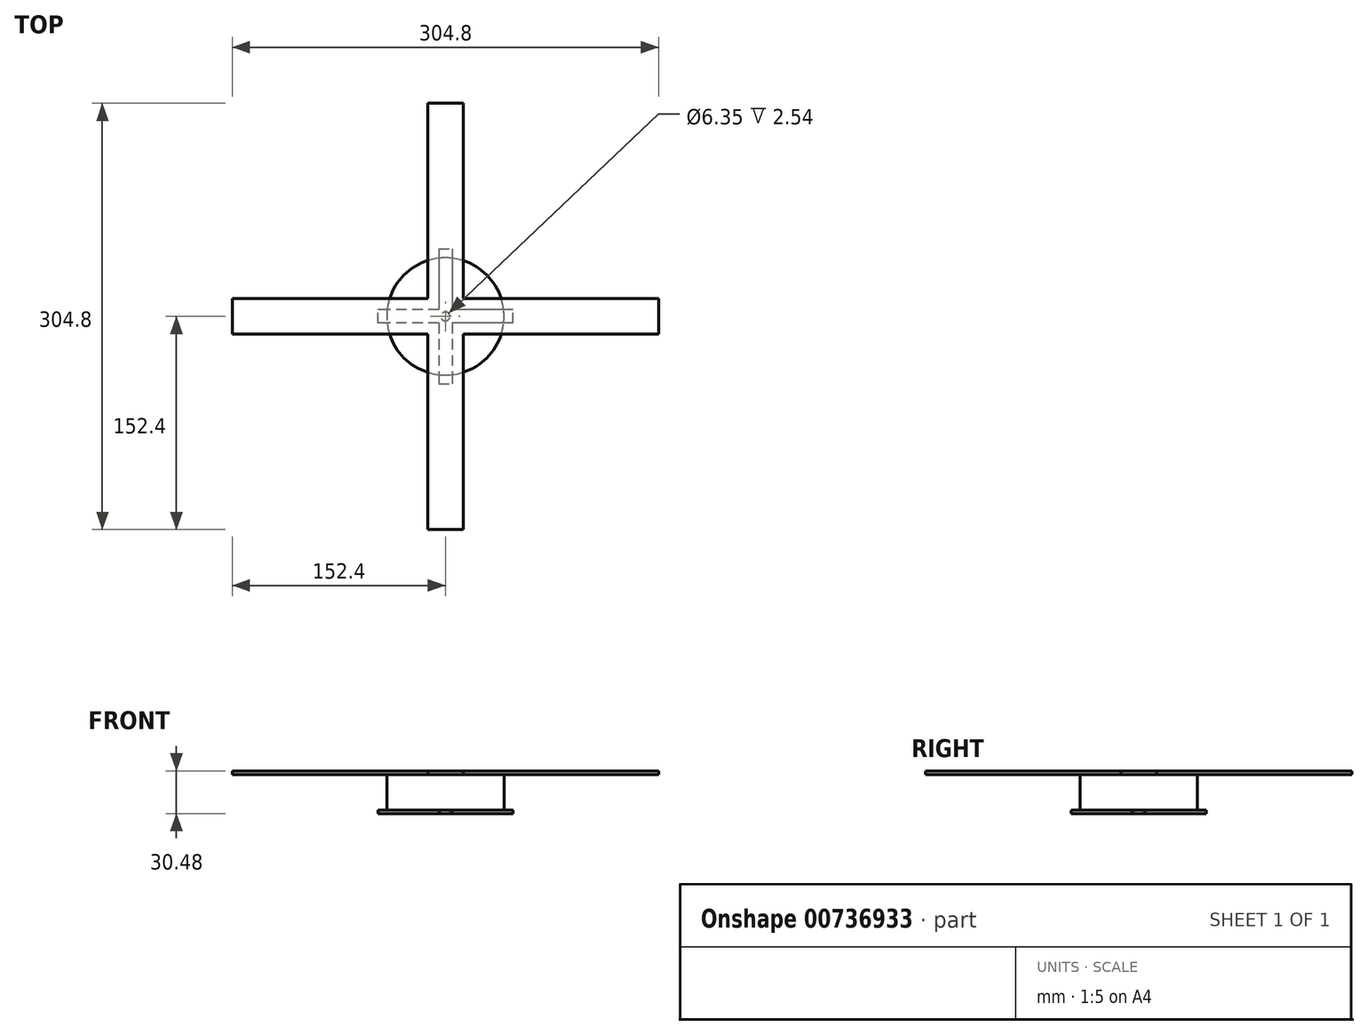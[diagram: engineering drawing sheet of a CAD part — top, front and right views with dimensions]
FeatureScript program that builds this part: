
annotation { "Feature Type Name" : "Feature", "Feature Type Description" : "" }
export const myFeature = defineFeature(function(context is Context, id is Id, definition is map)
    precondition{}
    {
        {
            var Q0;
            Q0=qCreatedBy(makeId("Top.planeOp"),FACE);
            var sketch = newSketch(context, id + "F0", { "sketchPlane" : qUnion([Q0])});
            skCircle(sketch, "E0", {"center": v(0, 0) * mm, "radius": 41.91 * mm});
            skSolve(sketch);
        }
        {
            var Q0;
            Q0=makeQuery(id+"F0.imprint","IMPRINT",FACE,{"disambiguationData":[TD([[makeQuery(id+"F0.imprint","IMPRINT",EDGE,{"derivedFrom":sQuery(id+"F0.wireOp",EDGE,"E0")}),1.0]])]});
            extrude(context, id + "F1", {"entities" : qUnion([Q0]), "depth" : 25.4 * mm, "offsetDistance" : 25.4 * mm});
        }
        {
            var Q0;
            Q0=makeQuery(id+"F1.opExtrude","CAP_FACE",FACE,{"disambiguationData":[OSD([sQuery(id+"F0.wireOp",EDGE,"E0")])],"isStart":false});
            var sketch = newSketch(context, id + "F2", { "sketchPlane" : qUnion([Q0])});
            skLineSegment(sketch, "E1.bottom", {"start": v(12.7, 152.4) * mm, "end": v(-12.7, 152.4) * mm});
            skLineSegment(sketch, "E1.top", {"start": v(12.7, -152.4) * mm, "end": v(-12.7, -152.4) * mm});
            skLineSegment(sketch, "E1.left", {"start": v(12.7, 152.4) * mm, "end": v(12.7, -152.4) * mm});
            skLineSegment(sketch, "E1.right", {"start": v(-12.7, 152.4) * mm, "end": v(-12.7, -152.4) * mm});
            skPoint(sketch, "E1.middle", {"position": v(0, 0) * mm});
            skLineSegment(sketch, "E2.bottom", {"start": v(152.4, -12.7) * mm, "end": v(-152.4, -12.7) * mm});
            skLineSegment(sketch, "E2.top", {"start": v(152.4, 12.7) * mm, "end": v(-152.4, 12.7) * mm});
            skLineSegment(sketch, "E2.left", {"start": v(152.4, -12.7) * mm, "end": v(152.4, 12.7) * mm});
            skLineSegment(sketch, "E2.right", {"start": v(-152.4, -12.7) * mm, "end": v(-152.4, 12.7) * mm});
            skSolve(sketch);
        }
        {
            var Q0;
            Q0 = qSketchRegion(id + "F2", true);
            extrude(context, id + "F3", {"entities" : qUnion([Q0]), "operationType" : NewBodyOperationType.ADD, "depth" : 2.54 * mm, "offsetDistance" : 25.4 * mm});
        }
        {
            var Q0;
            Q0=makeQuery(id+"F1.opExtrude","CAP_FACE",FACE,{"disambiguationData":[OSD([sQuery(id+"F0.wireOp",EDGE,"E0")])],"isStart":true});
            var sketch = newSketch(context, id + "F4", { "sketchPlane" : qUnion([Q0])});
            skLineSegment(sketch, "E3.bottom", {"start": v(-4.76, -48.26) * mm, "end": v(4.76, -48.26) * mm});
            skLineSegment(sketch, "E3.top", {"start": v(-4.76, 48.26) * mm, "end": v(4.76, 48.26) * mm});
            skLineSegment(sketch, "E3.left", {"start": v(-4.76, -48.26) * mm, "end": v(-4.76, 48.26) * mm});
            skLineSegment(sketch, "E3.right", {"start": v(4.76, -48.26) * mm, "end": v(4.76, 48.26) * mm});
            skPoint(sketch, "E3.middle", {"position": v(0, 0) * mm});
            skLineSegment(sketch, "E4.bottom", {"start": v(48.26, 4.76) * mm, "end": v(-48.26, 4.76) * mm});
            skLineSegment(sketch, "E4.top", {"start": v(48.26, -4.76) * mm, "end": v(-48.26, -4.76) * mm});
            skLineSegment(sketch, "E4.left", {"start": v(48.26, 4.76) * mm, "end": v(48.26, -4.76) * mm});
            skLineSegment(sketch, "E4.right", {"start": v(-48.26, 4.76) * mm, "end": v(-48.26, -4.76) * mm});
            skCircle(sketch, "E5", {"center": v(0, 0) * mm, "radius": 3.18 * mm});
            skSolve(sketch);
        }
        {
            var Q0;
            Q0 = qSketchRegion(id + "F4", true);
            extrude(context, id + "F5", {"entities" : qUnion([Q0]), "operationType" : NewBodyOperationType.ADD, "depth" : 2.54 * mm, "offsetDistance" : 25.4 * mm});
        }
    });
